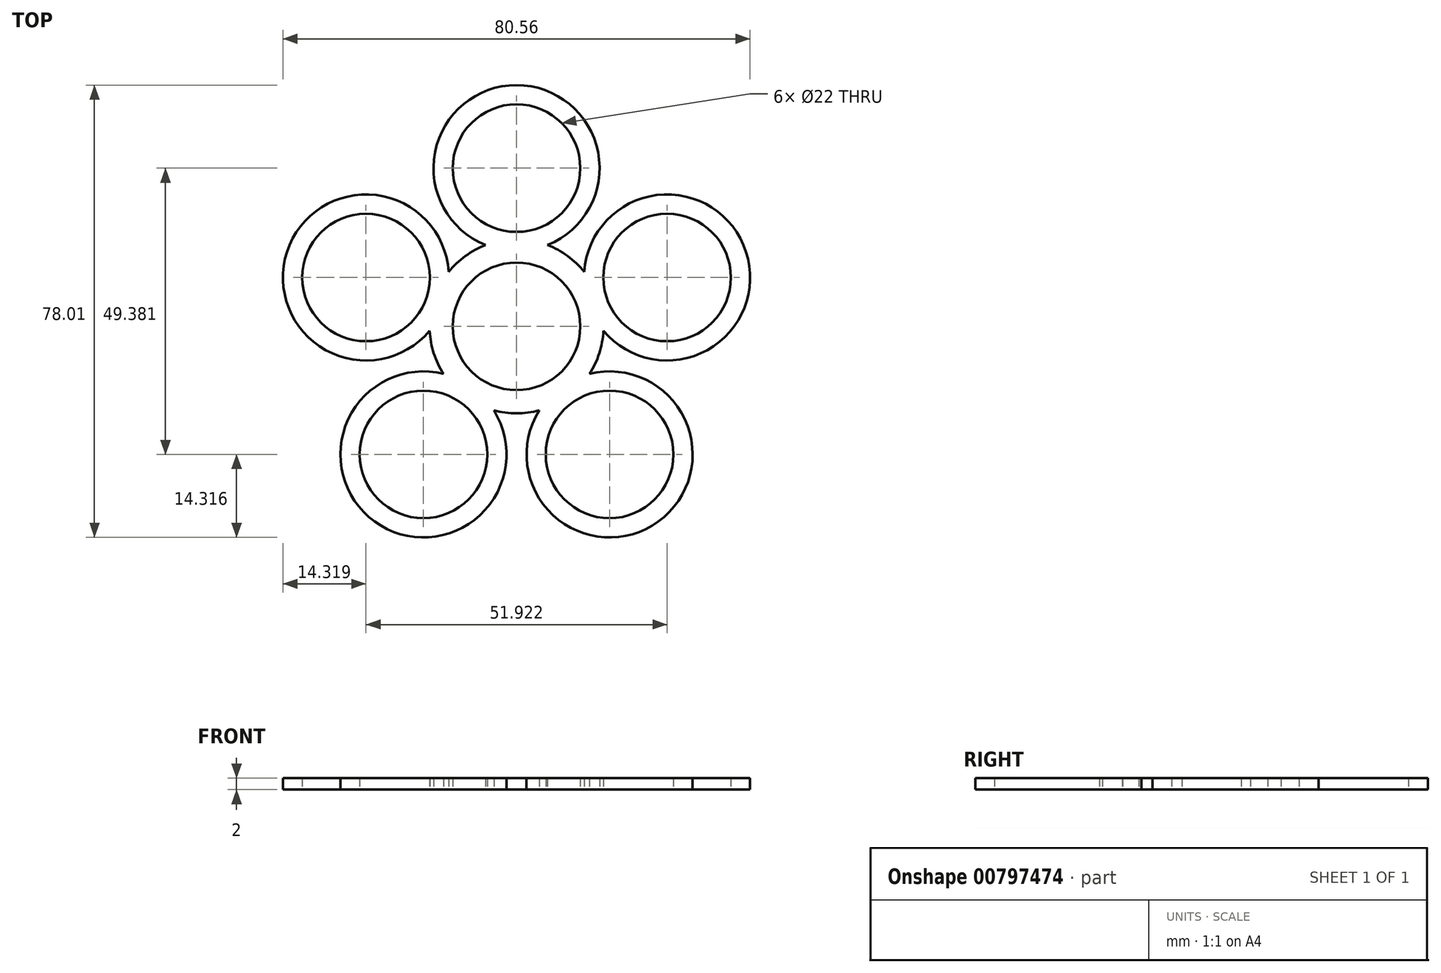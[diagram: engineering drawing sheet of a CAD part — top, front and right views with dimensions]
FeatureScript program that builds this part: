
annotation { "Feature Type Name" : "Feature", "Feature Type Description" : "" }
export const myFeature = defineFeature(function(context is Context, id is Id, definition is map)
    precondition{}
    {
        {
            var Q0;
            Q0=qCreatedBy(makeId("Top.planeOp"),FACE);
            var sketch = newSketch(context, id + "F0", { "sketchPlane" : qUnion([Q0])});
            skArc(sketch, "E0", {"start": v(5.77, 9.37) * mm, "mid": v(0, 11) * mm, "end": v(-5.77, 9.37) * mm});
            skArc(sketch, "E1", {"start": v(7.87, 12.77) * mm, "mid": v(6.64, 13.45) * mm, "end": v(5.35, 14.02) * mm});
            skCircle(sketch, "E2", {"center": v(0, 27.3) * mm, "radius": 14.32 * mm});
            skCircle(sketch, "E3", {"center": v(0, 27.3) * mm, "radius": 11 * mm});
            skArc(sketch, "E4.trimOffspring", {"start": v(-5.35, 14.02) * mm, "mid": v(-6.64, 13.45) * mm, "end": v(-7.87, 12.77) * mm});
            skCircle(sketch, "E5.1.0", {"center": v(-25.96, 8.44) * mm, "radius": 11 * mm});
            skArc(sketch, "E5.1.2", {"start": v(-14.98, -0.75) * mm, "mid": v(-14.84, -2.15) * mm, "end": v(-14.58, -3.54) * mm});
            skArc(sketch, "E5.1.3", {"start": v(-9.71, 11.43) * mm, "mid": v(-10.74, 10.47) * mm, "end": v(-11.68, 9.42) * mm});
            skCircle(sketch, "E5.1.4", {"center": v(-25.96, 8.44) * mm, "radius": 14.32 * mm});
            skArc(sketch, "E5.1.6", {"start": v(-7.12, 8.38) * mm, "mid": v(-10.46, 3.4) * mm, "end": v(-10.69, -2.6) * mm});
            skCircle(sketch, "E5.2.0", {"center": v(-16.04, -22.08) * mm, "radius": 11 * mm});
            skArc(sketch, "E5.2.2", {"start": v(-3.91, -14.48) * mm, "mid": v(-2.54, -14.78) * mm, "end": v(-1.14, -14.96) * mm});
            skArc(sketch, "E5.2.3", {"start": v(-13.87, -5.7) * mm, "mid": v(-13.28, -6.98) * mm, "end": v(-12.56, -8.2) * mm});
            skCircle(sketch, "E5.2.4", {"center": v(-16.04, -22.08) * mm, "radius": 14.32 * mm});
            skArc(sketch, "E5.2.6", {"start": v(-10.17, -4.19) * mm, "mid": v(-6.47, -8.9) * mm, "end": v(-0.84, -10.97) * mm});
            skCircle(sketch, "E6.3.3.0", {"center": v(16.04, -22.08) * mm, "radius": 11 * mm});
            skArc(sketch, "E6.5.3.0", {"start": v(12.56, -8.2) * mm, "mid": v(13.28, -6.98) * mm, "end": v(13.87, -5.7) * mm});
            skArc(sketch, "E6.9.3.0", {"start": v(1.14, -14.96) * mm, "mid": v(2.54, -14.78) * mm, "end": v(3.91, -14.48) * mm});
            skCircle(sketch, "E6.13.3.0", {"center": v(16.04, -22.08) * mm, "radius": 14.32 * mm});
            skArc(sketch, "E6.18.3.0", {"start": v(0.84, -10.97) * mm, "mid": v(6.47, -8.9) * mm, "end": v(10.17, -4.19) * mm});
            skCircle(sketch, "E6.3.4.0", {"center": v(25.96, 8.44) * mm, "radius": 11 * mm});
            skArc(sketch, "E6.5.4.0", {"start": v(11.68, 9.42) * mm, "mid": v(10.74, 10.47) * mm, "end": v(9.71, 11.43) * mm});
            skArc(sketch, "E6.9.4.0", {"start": v(14.58, -3.54) * mm, "mid": v(14.84, -2.15) * mm, "end": v(14.98, -0.75) * mm});
            skCircle(sketch, "E6.13.4.0", {"center": v(25.96, 8.44) * mm, "radius": 14.32 * mm});
            skArc(sketch, "E6.18.4.0", {"start": v(10.69, -2.6) * mm, "mid": v(10.46, 3.4) * mm, "end": v(7.12, 8.38) * mm});
            skArc(sketch, "E7", {"start": v(-10.17, -4.19) * mm, "mid": v(-10.46, -3.4) * mm, "end": v(-10.69, -2.6) * mm});
            skArc(sketch, "E8", {"start": v(-0.84, -10.97) * mm, "mid": v(0, -11) * mm, "end": v(0.84, -10.97) * mm});
            skArc(sketch, "E9", {"start": v(7.12, 8.38) * mm, "mid": v(6.47, 8.9) * mm, "end": v(5.77, 9.37) * mm});
            skArc(sketch, "E10", {"start": v(-5.77, 9.37) * mm, "mid": v(-6.47, 8.9) * mm, "end": v(-7.12, 8.38) * mm});
            skArc(sketch, "E11", {"start": v(-7.87, 12.77) * mm, "mid": v(-8.82, 12.14) * mm, "end": v(-9.71, 11.43) * mm});
            skArc(sketch, "E12", {"start": v(-14.58, -3.54) * mm, "mid": v(-14.27, -4.64) * mm, "end": v(-13.87, -5.7) * mm});
            skArc(sketch, "E13", {"start": v(10.17, -4.19) * mm, "mid": v(10.46, -3.4) * mm, "end": v(10.69, -2.6) * mm});
            skArc(sketch, "E14", {"start": v(-1.14, -14.96) * mm, "mid": v(0, -15) * mm, "end": v(1.14, -14.96) * mm});
            skArc(sketch, "E15", {"start": v(9.71, 11.43) * mm, "mid": v(8.82, 12.14) * mm, "end": v(7.87, 12.77) * mm});
            skArc(sketch, "E16", {"start": v(13.87, -5.7) * mm, "mid": v(14.27, -4.64) * mm, "end": v(14.58, -3.54) * mm});
            skSolve(sketch);
        }
        {
            var Q0;
            Q0 = qSketchRegion(id + "F0", true);
            extrude(context, id + "F1", {"entities" : qUnion([Q0]), "depth" : 2 * mm, "offsetDistance" : 25 * mm});
        }
    });
